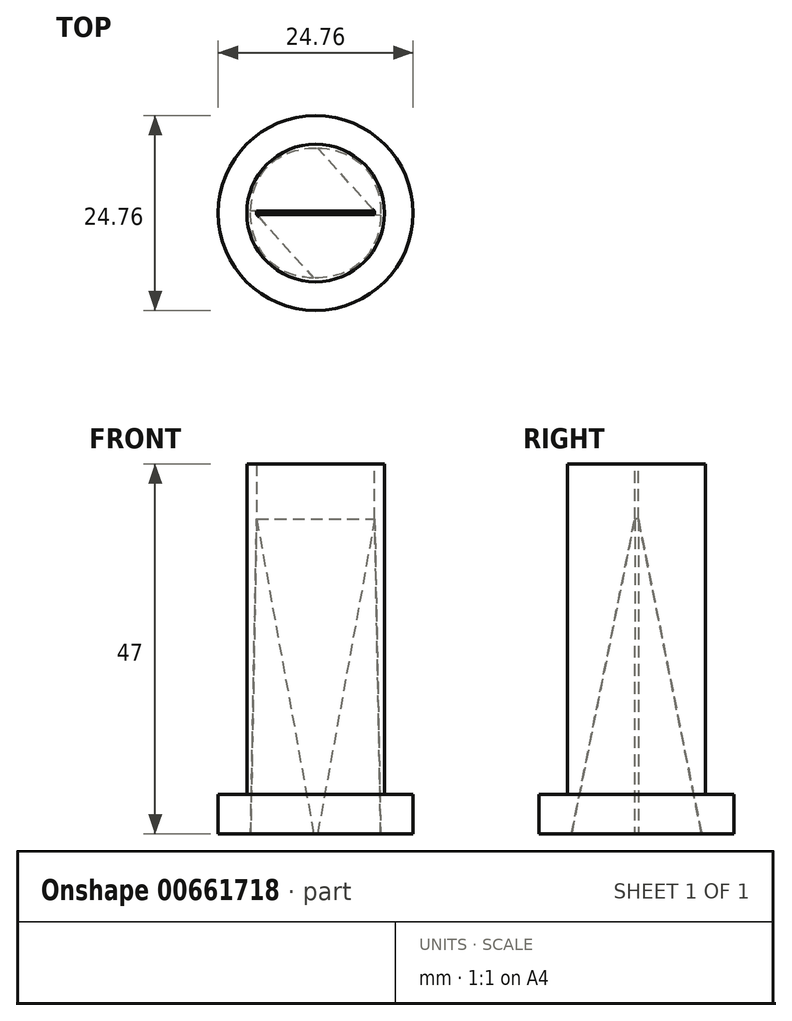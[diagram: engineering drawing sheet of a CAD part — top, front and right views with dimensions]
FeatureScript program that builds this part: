
annotation { "Feature Type Name" : "Feature", "Feature Type Description" : "" }
export const myFeature = defineFeature(function(context is Context, id is Id, definition is map)
    precondition{}
    {
        {
            var Q0;
            Q0=qCreatedBy(makeId("Top.planeOp"),FACE);
            var sketch = newSketch(context, id + "F0", { "sketchPlane" : qUnion([Q0])});
            skCircle(sketch, "E0", {"center": v(0, 0) * mm, "radius": 12.38 * mm});
            skSolve(sketch);
        }
        {
            var Q0;
            Q0=makeQuery(id+"F0.imprint","IMPRINT",FACE,{"disambiguationData":[TD([[makeQuery(id+"F0.imprint","IMPRINT",EDGE,{"derivedFrom":sQuery(id+"F0.wireOp",EDGE,"E0")}),1.0]])]});
            extrude(context, id + "F1", {"entities" : qUnion([Q0]), "depth" : 5 * mm, "offsetDistance" : 25 * mm});
        }
        {
            var Q0;
            Q0=makeQuery(id+"F1.opExtrude","CAP_FACE",FACE,{"disambiguationData":[OSD([sQuery(id+"F0.wireOp",EDGE,"E0")])],"isStart":false});
            var sketch = newSketch(context, id + "F2", { "sketchPlane" : qUnion([Q0])});
            skCircle(sketch, "E1", {"center": v(0, 0) * mm, "radius": 8.75 * mm});
            skSolve(sketch);
        }
        {
            var Q0;
            Q0=qSketchRegion(id+"F2",true);
            extrude(context, id + "F3", {"entities" : qUnion([Q0]), "operationType" : NewBodyOperationType.ADD, "depth" : 35 * mm, "offsetDistance" : 25 * mm});
        }
        {
            var Q0;
            Q0=makeQuery(id+"F3.opExtrude","CAP_FACE",FACE,{"disambiguationData":[OSD([sQuery(id+"F2.wireOp",EDGE,"E1")])],"isStart":false});
            var sketch = newSketch(context, id + "F4", { "sketchPlane" : qUnion([Q0])});
            skLineSegment(sketch, "E2.bottom", {"start": v(-7.5, 0.22) * mm, "end": v(7.5, 0.22) * mm});
            skLineSegment(sketch, "E2.top", {"start": v(-7.5, -0.22) * mm, "end": v(7.5, -0.22) * mm});
            skLineSegment(sketch, "E2.left", {"start": v(-7.5, 0.22) * mm, "end": v(-7.5, -0.22) * mm});
            skLineSegment(sketch, "E2.right", {"start": v(7.5, 0.22) * mm, "end": v(7.5, -0.22) * mm});
            skPoint(sketch, "E2.middle", {"position": v(0, 0) * mm});
            skSolve(sketch);
        }
        {
            var Q0;
            Q0=makeQuery(id+"F1.opExtrude","CAP_FACE",FACE,{"disambiguationData":[OSD([sQuery(id+"F0.wireOp",EDGE,"E0")])],"isStart":true});
            var sketch = newSketch(context, id + "F5", { "sketchPlane" : qUnion([Q0])});
            skPoint(sketch, "E3.middle", {"position": v(0, 0) * mm});
            skFitSpline(sketch, "E4", {"points": [v(-6.01, 6.01) * mm, v(-6.01, -6.01) * mm, v(6.01, -6.01) * mm, v(6.01, 6.01) * mm, v(-6.01, 6.01) * mm]});
            skSolve(sketch);
        }
        {
            var Q1;
            Q1=qSketchRegion(id+"F4",true);
            var Q2;
            Q2=qSketchRegion(id+"F5",true);
            loft(context, id + "F6", {"operationType" : NewBodyOperationType.REMOVE, "sheetProfilesArray" : [{ "sheetProfileEntities" : qUnion([Q1]) }, { "sheetProfileEntities" : qUnion([Q2]) }]});
        }
        {
            var Q0;
            Q0=makeQuery(id+"F3.opExtrude","CAP_FACE",FACE,{"disambiguationData":[OSD([sQuery(id+"F2.wireOp",EDGE,"E1")])],"isStart":false});
            extrude(context, id + "F7", {"entities" : qUnion([Q0]), "operationType" : NewBodyOperationType.ADD, "depth" : 7 * mm, "offsetDistance" : 25 * mm});
        }
    });
